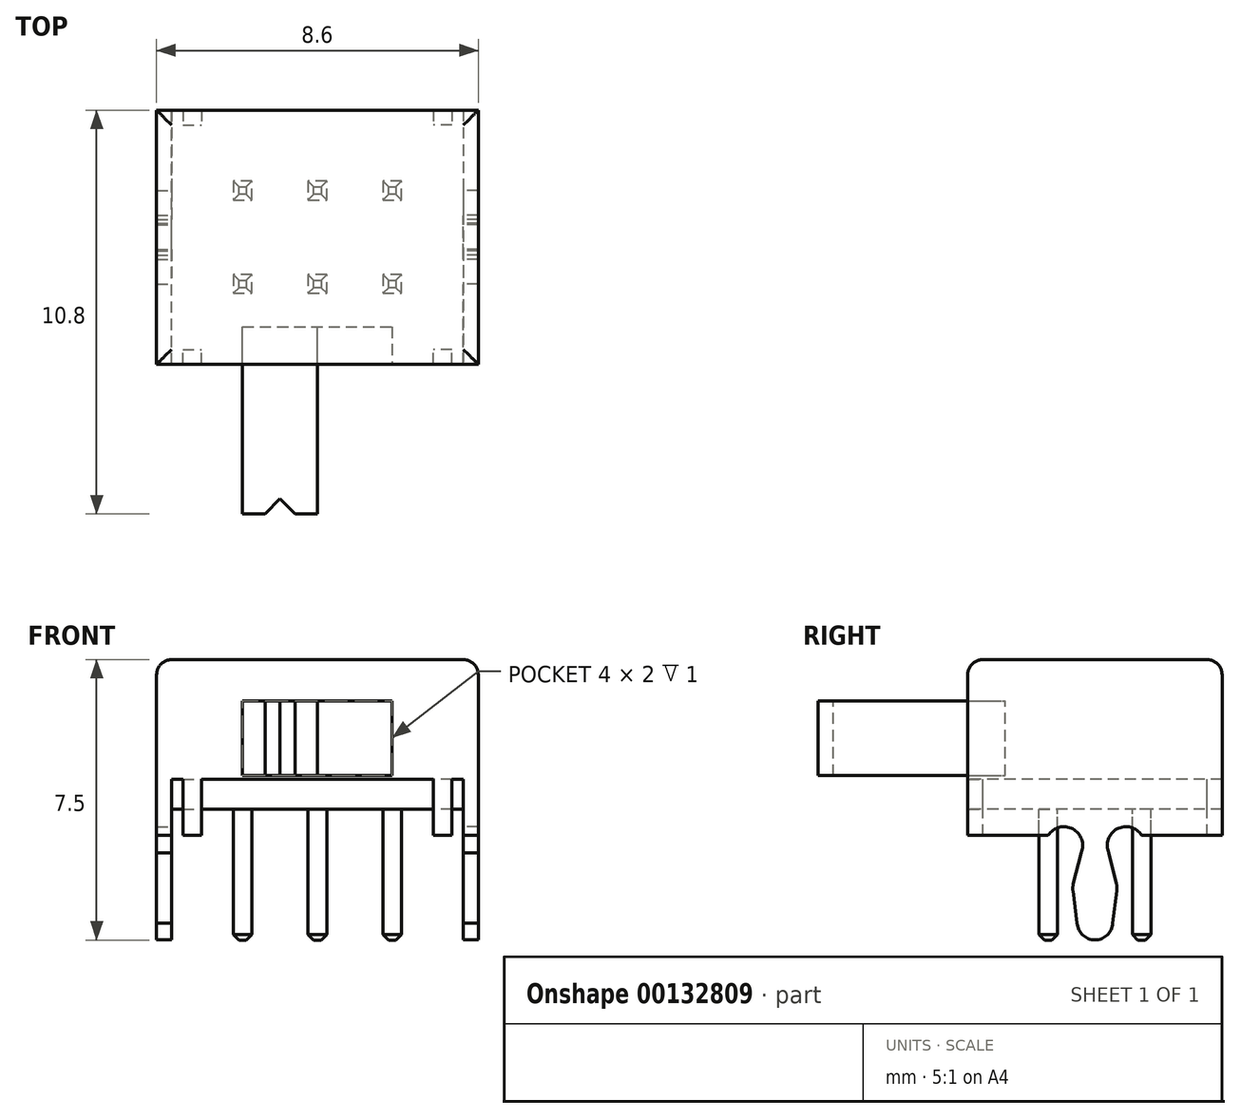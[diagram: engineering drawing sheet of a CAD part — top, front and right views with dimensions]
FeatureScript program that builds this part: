
annotation { "Feature Type Name" : "Feature", "Feature Type Description" : "" }
export const myFeature = defineFeature(function(context is Context, id is Id, definition is map)
    precondition{}
    {
        {
            var Q0;
            Q0=qCreatedBy(makeId("Right.planeOp"),FACE);
            var sketch = newSketch(context, id + "F0", { "sketchPlane" : qUnion([Q0])});
            skLineSegment(sketch, "E0", {"start": v(-3.4, 0) * mm, "end": v(-3.4, 4.7) * mm});
            skLineSegment(sketch, "E1", {"start": v(-3.4, 4.7) * mm, "end": v(3.4, 4.7) * mm});
            skLineSegment(sketch, "E2", {"start": v(3.4, 4.7) * mm, "end": v(3.4, 0) * mm});
            skLineSegment(sketch, "E3", {"start": v(3.4, 0) * mm, "end": v(1.25, 0) * mm});
            skLineSegment(sketch, "E4", {"start": v(-3.4, 0) * mm, "end": v(-1.25, 0) * mm});
            skArc(sketch, "E5", {"start": v(-0.37, -0.47) * mm, "mid": v(-0.6, 0.17) * mm, "end": v(-1.25, 0) * mm});
            skLineSegment(sketch, "E6", {"start": v(-0.37, -0.47) * mm, "end": v(-0.58, -1.3) * mm});
            skLineSegment(sketch, "E7", {"start": v(-0.59, -1.48) * mm, "end": v(-0.48, -2.35) * mm});
            skArc(sketch, "E8.MirrorCS", {"start": v(0.37, -0.47) * mm, "mid": v(0.6, 0.17) * mm, "end": v(1.25, 0) * mm});
            skLineSegment(sketch, "E9.MirrorCS", {"start": v(0.59, -1.48) * mm, "end": v(0.48, -2.35) * mm});
            skLineSegment(sketch, "E10.MirrorCS", {"start": v(0.37, -0.47) * mm, "end": v(0.58, -1.3) * mm});
            skArc(sketch, "E11", {"start": v(-0.48, -2.35) * mm, "mid": v(0, -2.8) * mm, "end": v(0.48, -2.35) * mm});
            skPoint(sketch, "E12.visualSharp", {"position": v(-0.6, -1.39) * mm});
            skArc(sketch, "E12.filletArc", {"start": v(-0.58, -1.3) * mm, "mid": v(-0.6, -1.39) * mm, "end": v(-0.59, -1.48) * mm});
            skPoint(sketch, "E13.visualSharp", {"position": v(0.6, -1.39) * mm});
            skArc(sketch, "E13.filletArc", {"start": v(0.59, -1.48) * mm, "mid": v(0.6, -1.39) * mm, "end": v(0.58, -1.3) * mm});
            skSolve(sketch);
        }
        {
            var Q0;
            Q0=makeQuery(id+"F0.imprint","IMPRINT",FACE,{"disambiguationData":[TD([[makeQuery(id+"F0.imprint","IMPRINT",EDGE,{"derivedFrom":sQuery(id+"F0.wireOp",EDGE,"E0")}),-1.0]])]});
            extrude(context, id + "F1", {"entities" : qUnion([Q0]), "depth" : 4.3 * mm, "hasSecondDirection" : true, "secondDirectionOppositeDirection" : false, "secondDirectionDepth" : 3.9 * mm});
        }
        {
            var Q0;
            Q0=makeQuery(id+"F1.opExtrude","SWEPT_BODY",BODY,{"disambiguationData":[OSD([sQuery(id+"F0.wireOp",EDGE,"E0"),sQuery(id+"F0.wireOp",EDGE,"E1"),sQuery(id+"F0.wireOp",EDGE,"E2"),sQuery(id+"F0.wireOp",EDGE,"E3"),sQuery(id+"F0.wireOp",EDGE,"E4"),sQuery(id+"F0.wireOp",EDGE,"E5"),sQuery(id+"F0.wireOp",EDGE,"E6"),sQuery(id+"F0.wireOp",EDGE,"E7"),sQuery(id+"F0.wireOp",EDGE,"E8.MirrorCS"),sQuery(id+"F0.wireOp",EDGE,"E9.MirrorCS"),sQuery(id+"F0.wireOp",EDGE,"E10.MirrorCS"),sQuery(id+"F0.wireOp",EDGE,"E11"),sQuery(id+"F0.wireOp",EDGE,"E12.filletArc"),sQuery(id+"F0.wireOp",EDGE,"E13.filletArc")])]});
            var Q1;
            Q1=qCreatedBy(makeId("Right.planeOp"),FACE);
            mirror(context, id + "F2", {"entities" : qUnion([Q0]), "mirrorPlane" : qUnion([Q1])});
        }
        {
            var Q0;
            Q0=makeQuery(id+"F2.opPattern","COPY",FACE,{"derivedFrom":makeQuery(id+"F1.opExtrude","CAP_FACE",FACE,{"disambiguationData":[OSD([sQuery(id+"F0.wireOp",EDGE,"E0"),sQuery(id+"F0.wireOp",EDGE,"E1"),sQuery(id+"F0.wireOp",EDGE,"E2"),sQuery(id+"F0.wireOp",EDGE,"E3"),sQuery(id+"F0.wireOp",EDGE,"E4"),sQuery(id+"F0.wireOp",EDGE,"E5"),sQuery(id+"F0.wireOp",EDGE,"E6"),sQuery(id+"F0.wireOp",EDGE,"E7"),sQuery(id+"F0.wireOp",EDGE,"E8.MirrorCS"),sQuery(id+"F0.wireOp",EDGE,"E9.MirrorCS"),sQuery(id+"F0.wireOp",EDGE,"E10.MirrorCS"),sQuery(id+"F0.wireOp",EDGE,"E11"),sQuery(id+"F0.wireOp",EDGE,"E12.filletArc"),sQuery(id+"F0.wireOp",EDGE,"E13.filletArc")])],"isStart":true}),"instanceName":"1"});
            var sketch = newSketch(context, id + "F3", { "sketchPlane" : qUnion([Q0])});
            skLineSegment(sketch, "E14.bottom", {"start": v(-3.4, 4.7) * mm, "end": v(3.4, 4.7) * mm});
            skLineSegment(sketch, "E14.top", {"start": v(-3.4, 1.5) * mm, "end": v(3.4, 1.5) * mm});
            skLineSegment(sketch, "E14.left", {"start": v(-3.4, 4.7) * mm, "end": v(-3.4, 1.5) * mm});
            skLineSegment(sketch, "E14.right", {"start": v(3.4, 4.7) * mm, "end": v(3.4, 1.5) * mm});
            skSolve(sketch);
        }
        {
            var Q0;
            Q0=makeQuery(id+"F3.imprint","IMPRINT",FACE,{"disambiguationData":[TD([[makeQuery(id+"F3.imprint","IMPRINT",EDGE,{"derivedFrom":sQuery(id+"F3.wireOp",EDGE,"E14.bottom")}),-1.0]])]});
            extrude(context, id + "F4", {"entities" : qUnion([Q0]), "operationType" : NewBodyOperationType.ADD, "depth" : 8 * mm});
        }
        {
            var Q0;
            Q0=makeQuery(id+"F4.opExtrude","SWEPT_FACE",FACE,{"disambiguationData":[OSD([sQuery(id+"F3.wireOp",EDGE,"E14.top")])]});
            var sketch = newSketch(context, id + "F5", { "sketchPlane" : qUnion([Q0])});
            skLineSegment(sketch, "E15.bottom", {"start": v(3.6, 3.4) * mm, "end": v(3.1, 3.4) * mm});
            skLineSegment(sketch, "E15.top", {"start": v(3.6, 3) * mm, "end": v(3.1, 3) * mm});
            skLineSegment(sketch, "E15.left", {"start": v(3.6, 3.4) * mm, "end": v(3.6, 3) * mm});
            skLineSegment(sketch, "E15.right", {"start": v(3.1, 3.4) * mm, "end": v(3.1, 3) * mm});
            skLineSegment(sketch, "E16.bottom", {"start": v(-3.6, 3.4) * mm, "end": v(-3.1, 3.4) * mm});
            skLineSegment(sketch, "E16.top", {"start": v(-3.6, 3) * mm, "end": v(-3.1, 3) * mm});
            skLineSegment(sketch, "E16.left", {"start": v(-3.6, 3.4) * mm, "end": v(-3.6, 3) * mm});
            skLineSegment(sketch, "E16.right", {"start": v(-3.1, 3.4) * mm, "end": v(-3.1, 3) * mm});
            skLineSegment(sketch, "E17.bottom", {"start": v(-3.6, -3.4) * mm, "end": v(-3.1, -3.4) * mm});
            skLineSegment(sketch, "E17.top", {"start": v(-3.6, -3) * mm, "end": v(-3.1, -3) * mm});
            skLineSegment(sketch, "E17.left", {"start": v(-3.6, -3.4) * mm, "end": v(-3.6, -3) * mm});
            skLineSegment(sketch, "E17.right", {"start": v(-3.1, -3.4) * mm, "end": v(-3.1, -3) * mm});
            skLineSegment(sketch, "E18.bottom", {"start": v(3.6, -3.4) * mm, "end": v(3.1, -3.4) * mm});
            skLineSegment(sketch, "E18.top", {"start": v(3.6, -3) * mm, "end": v(3.1, -3) * mm});
            skLineSegment(sketch, "E18.left", {"start": v(3.6, -3.4) * mm, "end": v(3.6, -3) * mm});
            skLineSegment(sketch, "E18.right", {"start": v(3.1, -3.4) * mm, "end": v(3.1, -3) * mm});
            skSolve(sketch);
        }
        {
            var Q0;
            Q0=makeQuery(id+"F5.imprint","IMPRINT",FACE,{"disambiguationData":[TD([[makeQuery(id+"F5.imprint","IMPRINT",EDGE,{"derivedFrom":sQuery(id+"F5.wireOp",EDGE,"E15.bottom")}),1.0]])]});
            var Q1;
            Q1=makeQuery(id+"F5.imprint","IMPRINT",FACE,{"disambiguationData":[TD([[makeQuery(id+"F5.imprint","IMPRINT",EDGE,{"derivedFrom":sQuery(id+"F5.wireOp",EDGE,"E18.bottom")}),-1.0]])]});
            var Q2;
            Q2=makeQuery(id+"F5.imprint","IMPRINT",FACE,{"disambiguationData":[TD([[makeQuery(id+"F5.imprint","IMPRINT",EDGE,{"derivedFrom":sQuery(id+"F5.wireOp",EDGE,"E16.bottom")}),1.0]])]});
            var Q3;
            Q3=makeQuery(id+"F5.imprint","IMPRINT",FACE,{"disambiguationData":[TD([[makeQuery(id+"F5.imprint","IMPRINT",EDGE,{"derivedFrom":sQuery(id+"F5.wireOp",EDGE,"E17.bottom")}),-1.0]])]});
            extrude(context, id + "F6", {"entities" : qUnion([Q0, Q1, Q2, Q3]), "operationType" : NewBodyOperationType.ADD, "depth" : 1.5 * mm});
        }
        {
            var Q0;
            Q0=makeQuery(id+"F4.opExtrude","SWEPT_FACE",FACE,{"disambiguationData":[OSD([sQuery(id+"F3.wireOp",EDGE,"E14.top")])]});
            extrude(context, id + "F7", {"entities" : qUnion([Q0]), "depth" : .8 * mm});
        }
        {
            var Q0;
            {var subQ0=makeQuery(id+"F1.opExtrude","SWEPT_FACE",FACE,{"disambiguationData":[OSD([sQuery(id+"F0.wireOp",EDGE,"E1")])]});Q0=makeQuery(id+"F4.boolean.opBoolean","MERGE",FACE,{"derivedFrom":[subQ0,makeQuery(id+"F2.opPattern","COPY",FACE,{"derivedFrom":subQ0,"instanceName":"1"}),makeQuery(id+"F4.opExtrude","SWEPT_FACE",FACE,{"disambiguationData":[OSD([sQuery(id+"F3.wireOp",EDGE,"E14.bottom")])]})]});}
            fillet(context, id + "F8", {"entities" : qUnion([Q0]), "radius" : 0.4 * mm, "tangentPropagation" : true, "allowEdgeOverflow" : false});
        }
        {
            var Q0;
            {var subQ0=makeQuery(id+"F1.opExtrude","SWEPT_FACE",FACE,{"disambiguationData":[OSD([sQuery(id+"F0.wireOp",EDGE,"E0")])]});Q0=makeQuery(id+"F6.boolean.opBoolean","MERGE",FACE,{"derivedFrom":[makeQuery(id+"F4.boolean.opBoolean","MERGE",FACE,{"derivedFrom":[subQ0,makeQuery(id+"F2.opPattern","COPY",FACE,{"derivedFrom":subQ0,"instanceName":"1"}),makeQuery(id+"F4.opExtrude","SWEPT_FACE",FACE,{"disambiguationData":[OSD([sQuery(id+"F3.wireOp",EDGE,"E14.left")])]})]}),makeQuery(id+"F6.opExtrude","SWEPT_FACE",FACE,{"disambiguationData":[OSD([sQuery(id+"F5.wireOp",EDGE,"E15.bottom")])]}),makeQuery(id+"F6.opExtrude","SWEPT_FACE",FACE,{"disambiguationData":[OSD([sQuery(id+"F5.wireOp",EDGE,"E16.bottom")])]})]});}
            var sketch = newSketch(context, id + "F9", { "sketchPlane" : qUnion([Q0])});
            skLineSegment(sketch, "E19.bottom", {"start": v(-2, 3.6) * mm, "end": v(2, 3.6) * mm});
            skLineSegment(sketch, "E19.top", {"start": v(-2, 1.6) * mm, "end": v(2, 1.6) * mm});
            skLineSegment(sketch, "E19.left", {"start": v(-2, 3.6) * mm, "end": v(-2, 1.6) * mm});
            skLineSegment(sketch, "E19.right", {"start": v(2, 3.6) * mm, "end": v(2, 1.6) * mm});
            skSolve(sketch);
        }
        {
            var Q0;
            Q0=makeQuery(id+"F9.imprint","IMPRINT",FACE,{"disambiguationData":[TD([[makeQuery(id+"F9.imprint","IMPRINT",EDGE,{"derivedFrom":sQuery(id+"F9.wireOp",EDGE,"E19.bottom")}),-1.0]])]});
            extrude(context, id + "F10", {"entities" : qUnion([Q0]), "operationType" : NewBodyOperationType.REMOVE, "oppositeDirection" : true, "depth" : 1 * mm});
        }
        {
            var Q0;
            Q0=makeQuery(id+"F10.boolean.opBoolean","COPY",FACE,{"derivedFrom":makeQuery(id+"F10.opExtrude","CAP_FACE",FACE,{"disambiguationData":[OSD([sQuery(id+"F9.wireOp",EDGE,"E19.bottom"),sQuery(id+"F9.wireOp",EDGE,"E19.top"),sQuery(id+"F9.wireOp",EDGE,"E19.left"),sQuery(id+"F9.wireOp",EDGE,"E19.right")])],"isStart":false})});
            var sketch = newSketch(context, id + "F11", { "sketchPlane" : qUnion([Q0])});
            skLineSegment(sketch, "E20.bottom", {"start": v(-2, 1.6) * mm, "end": v(0, 1.6) * mm});
            skLineSegment(sketch, "E20.top", {"start": v(-2, 3.6) * mm, "end": v(0, 3.6) * mm});
            skLineSegment(sketch, "E20.left", {"start": v(-2, 1.6) * mm, "end": v(-2, 3.6) * mm});
            skLineSegment(sketch, "E20.right", {"start": v(0, 1.6) * mm, "end": v(0, 3.6) * mm});
            skSolve(sketch);
        }
        {
            var Q0;
            Q0=makeQuery(id+"F11.imprint","IMPRINT",FACE,{"disambiguationData":[TD([[makeQuery(id+"F11.imprint","IMPRINT",EDGE,{"derivedFrom":sQuery(id+"F11.wireOp",EDGE,"E20.bottom")}),1.0]])]});
            extrude(context, id + "F12", {"entities" : qUnion([Q0]), "depth" : 5 * mm});
        }
        {
            var Q0;
            Q0=makeQuery(id+"F12.opExtrude","SWEPT_FACE",FACE,{"disambiguationData":[OSD([sQuery(id+"F11.wireOp",EDGE,"E20.top")])]});
            var sketch = newSketch(context, id + "F13", { "sketchPlane" : qUnion([Q0])});
            skLineSegment(sketch, "E21", {"start": v(-1.4, -7.4) * mm, "end": v(-1, -7) * mm});
            skLineSegment(sketch, "E22", {"start": v(-1, -7) * mm, "end": v(-0.6, -7.4) * mm});
            skLineSegment(sketch, "E23", {"start": v(-0.6, -7.4) * mm, "end": v(-1.4, -7.4) * mm});
            skSolve(sketch);
        }
        {
            var Q0;
            Q0=makeQuery(id+"F13.imprint","IMPRINT",FACE,{"disambiguationData":[TD([[makeQuery(id+"F13.imprint","IMPRINT",EDGE,{"derivedFrom":sQuery(id+"F13.wireOp",EDGE,"E21")}),-1.0]])]});
            extrude(context, id + "F14", {"entities" : qUnion([Q0]), "operationType" : NewBodyOperationType.REMOVE, "oppositeDirection" : true, "depth" : 25 * mm});
        }
        {
            var Q0;
            Q0=makeQuery(id+"F7.opExtrude","CAP_FACE",FACE,{"disambiguationData":[OSD([sQuery(id+"F3.wireOp",EDGE,"E14.top")])],"isStart":false});
            var sketch = newSketch(context, id + "F15", { "sketchPlane" : qUnion([Q0])});
            skLineSegment(sketch, "E24.bottom", {"start": v(-0.25, 1.5) * mm, "end": v(0.25, 1.5) * mm});
            skLineSegment(sketch, "E24.top", {"start": v(-0.25, 1) * mm, "end": v(0.25, 1) * mm});
            skLineSegment(sketch, "E24.left", {"start": v(-0.25, 1.5) * mm, "end": v(-0.25, 1) * mm});
            skLineSegment(sketch, "E24.right", {"start": v(0.25, 1.5) * mm, "end": v(0.25, 1) * mm});
            skPoint(sketch, "E25.oppositeSnap0", {"position": v(0, 1) * mm});
            skLineSegment(sketch, "E25.bottom", {"start": v(-1.75, 1.5) * mm, "end": v(-2.25, 1.5) * mm});
            skLineSegment(sketch, "E25.top", {"start": v(-1.75, 1) * mm, "end": v(-2.25, 1) * mm});
            skLineSegment(sketch, "E25.left", {"start": v(-1.75, 1.5) * mm, "end": v(-1.75, 1) * mm});
            skLineSegment(sketch, "E25.right", {"start": v(-2.25, 1.5) * mm, "end": v(-2.25, 1) * mm});
            skLineSegment(sketch, "E26.bottom", {"start": v(1.75, 1.5) * mm, "end": v(2.25, 1.5) * mm});
            skLineSegment(sketch, "E26.top", {"start": v(1.75, 1) * mm, "end": v(2.25, 1) * mm});
            skLineSegment(sketch, "E26.left", {"start": v(1.75, 1.5) * mm, "end": v(1.75, 1) * mm});
            skLineSegment(sketch, "E26.right", {"start": v(2.25, 1.5) * mm, "end": v(2.25, 1) * mm});
            skLineSegment(sketch, "E27.MirrorCS", {"start": v(-0.25, -1) * mm, "end": v(0.25, -1) * mm});
            skPoint(sketch, "E28.MirrorP", {"position": v(0, -1) * mm});
            skLineSegment(sketch, "E29.MirrorCS", {"start": v(2.25, -1.5) * mm, "end": v(2.25, -1) * mm});
            skLineSegment(sketch, "E30.MirrorCS", {"start": v(1.75, -1.5) * mm, "end": v(1.75, -1) * mm});
            skLineSegment(sketch, "E31.MirrorCS", {"start": v(1.75, -1) * mm, "end": v(2.25, -1) * mm});
            skLineSegment(sketch, "E32.MirrorCS", {"start": v(-0.25, -1.5) * mm, "end": v(0.25, -1.5) * mm});
            skLineSegment(sketch, "E33.MirrorCS", {"start": v(-0.25, -1.5) * mm, "end": v(-0.25, -1) * mm});
            skLineSegment(sketch, "E34.MirrorCS", {"start": v(1.75, -1.5) * mm, "end": v(2.25, -1.5) * mm});
            skLineSegment(sketch, "E35.MirrorCS", {"start": v(-2.25, -1.5) * mm, "end": v(-2.25, -1) * mm});
            skLineSegment(sketch, "E36.MirrorCS", {"start": v(-1.75, -1.5) * mm, "end": v(-1.75, -1) * mm});
            skLineSegment(sketch, "E37.MirrorCS", {"start": v(-1.75, -1) * mm, "end": v(-2.25, -1) * mm});
            skLineSegment(sketch, "E38.MirrorCS", {"start": v(0.25, -1.5) * mm, "end": v(0.25, -1) * mm});
            skLineSegment(sketch, "E39.MirrorCS", {"start": v(-1.75, -1.5) * mm, "end": v(-2.25, -1.5) * mm});
            skSolve(sketch);
        }
        {
            var Q0;
            Q0=makeQuery(id+"F15.imprint","IMPRINT",FACE,{"disambiguationData":[TD([[makeQuery(id+"F15.imprint","IMPRINT",EDGE,{"derivedFrom":sQuery(id+"F15.wireOp",EDGE,"E25.bottom")}),1.0]])]});
            var Q1;
            Q1=makeQuery(id+"F15.imprint","IMPRINT",FACE,{"disambiguationData":[TD([[makeQuery(id+"F15.imprint","IMPRINT",EDGE,{"derivedFrom":sQuery(id+"F15.wireOp",EDGE,"E24.bottom")}),-1.0]])]});
            var Q2;
            Q2=makeQuery(id+"F15.imprint","IMPRINT",FACE,{"disambiguationData":[TD([[makeQuery(id+"F15.imprint","IMPRINT",EDGE,{"derivedFrom":sQuery(id+"F15.wireOp",EDGE,"E29.MirrorCS")}),1.0]])]});
            var Q3;
            Q3=makeQuery(id+"F15.imprint","IMPRINT",FACE,{"disambiguationData":[TD([[makeQuery(id+"F15.imprint","IMPRINT",EDGE,{"derivedFrom":sQuery(id+"F15.wireOp",EDGE,"E27.MirrorCS")}),-1.0]])]});
            var Q4;
            Q4=makeQuery(id+"F15.imprint","IMPRINT",FACE,{"disambiguationData":[TD([[makeQuery(id+"F15.imprint","IMPRINT",EDGE,{"derivedFrom":sQuery(id+"F15.wireOp",EDGE,"E35.MirrorCS")}),-1.0]])]});
            var Q5;
            Q5=makeQuery(id+"F15.imprint","IMPRINT",FACE,{"disambiguationData":[TD([[makeQuery(id+"F15.imprint","IMPRINT",EDGE,{"derivedFrom":sQuery(id+"F15.wireOp",EDGE,"E26.bottom")}),-1.0]])]});
            extrude(context, id + "F16", {"entities" : qUnion([Q0, Q1, Q2, Q3, Q4, Q5]), "depth" : 3.5 * mm});
        }
        {
            var Q0;
            Q0=makeQuery(id+"F16.opExtrude","CAP_FACE",FACE,{"disambiguationData":[OSD([sQuery(id+"F15.wireOp",EDGE,"E25.bottom"),sQuery(id+"F15.wireOp",EDGE,"E25.top"),sQuery(id+"F15.wireOp",EDGE,"E25.left"),sQuery(id+"F15.wireOp",EDGE,"E25.right")])],"isStart":false});
            var Q1;
            Q1=makeQuery(id+"F16.opExtrude","CAP_FACE",FACE,{"disambiguationData":[OSD([sQuery(id+"F15.wireOp",EDGE,"E24.bottom"),sQuery(id+"F15.wireOp",EDGE,"E24.top"),sQuery(id+"F15.wireOp",EDGE,"E24.left"),sQuery(id+"F15.wireOp",EDGE,"E24.right")])],"isStart":false});
            var Q2;
            Q2=makeQuery(id+"F16.opExtrude","CAP_FACE",FACE,{"disambiguationData":[OSD([sQuery(id+"F15.wireOp",EDGE,"E26.bottom"),sQuery(id+"F15.wireOp",EDGE,"E26.top"),sQuery(id+"F15.wireOp",EDGE,"E26.left"),sQuery(id+"F15.wireOp",EDGE,"E26.right")])],"isStart":false});
            var Q3;
            Q3=makeQuery(id+"F16.opExtrude","CAP_FACE",FACE,{"disambiguationData":[OSD([sQuery(id+"F15.wireOp",EDGE,"E29.MirrorCS"),sQuery(id+"F15.wireOp",EDGE,"E30.MirrorCS"),sQuery(id+"F15.wireOp",EDGE,"E31.MirrorCS"),sQuery(id+"F15.wireOp",EDGE,"E34.MirrorCS")])],"isStart":false});
            var Q4;
            Q4=makeQuery(id+"F16.opExtrude","CAP_FACE",FACE,{"disambiguationData":[OSD([sQuery(id+"F15.wireOp",EDGE,"E27.MirrorCS"),sQuery(id+"F15.wireOp",EDGE,"E32.MirrorCS"),sQuery(id+"F15.wireOp",EDGE,"E33.MirrorCS"),sQuery(id+"F15.wireOp",EDGE,"E38.MirrorCS")])],"isStart":false});
            var Q5;
            Q5=makeQuery(id+"F16.opExtrude","CAP_FACE",FACE,{"disambiguationData":[OSD([sQuery(id+"F15.wireOp",EDGE,"E35.MirrorCS"),sQuery(id+"F15.wireOp",EDGE,"E36.MirrorCS"),sQuery(id+"F15.wireOp",EDGE,"E37.MirrorCS"),sQuery(id+"F15.wireOp",EDGE,"E39.MirrorCS")])],"isStart":false});
            chamfer(context, id + "F17", {"entities" : qUnion([Q0, Q1, Q2, Q3, Q4, Q5]), "width" : 0.15 * mm, "tangentPropagation" : true});
        }
    });
